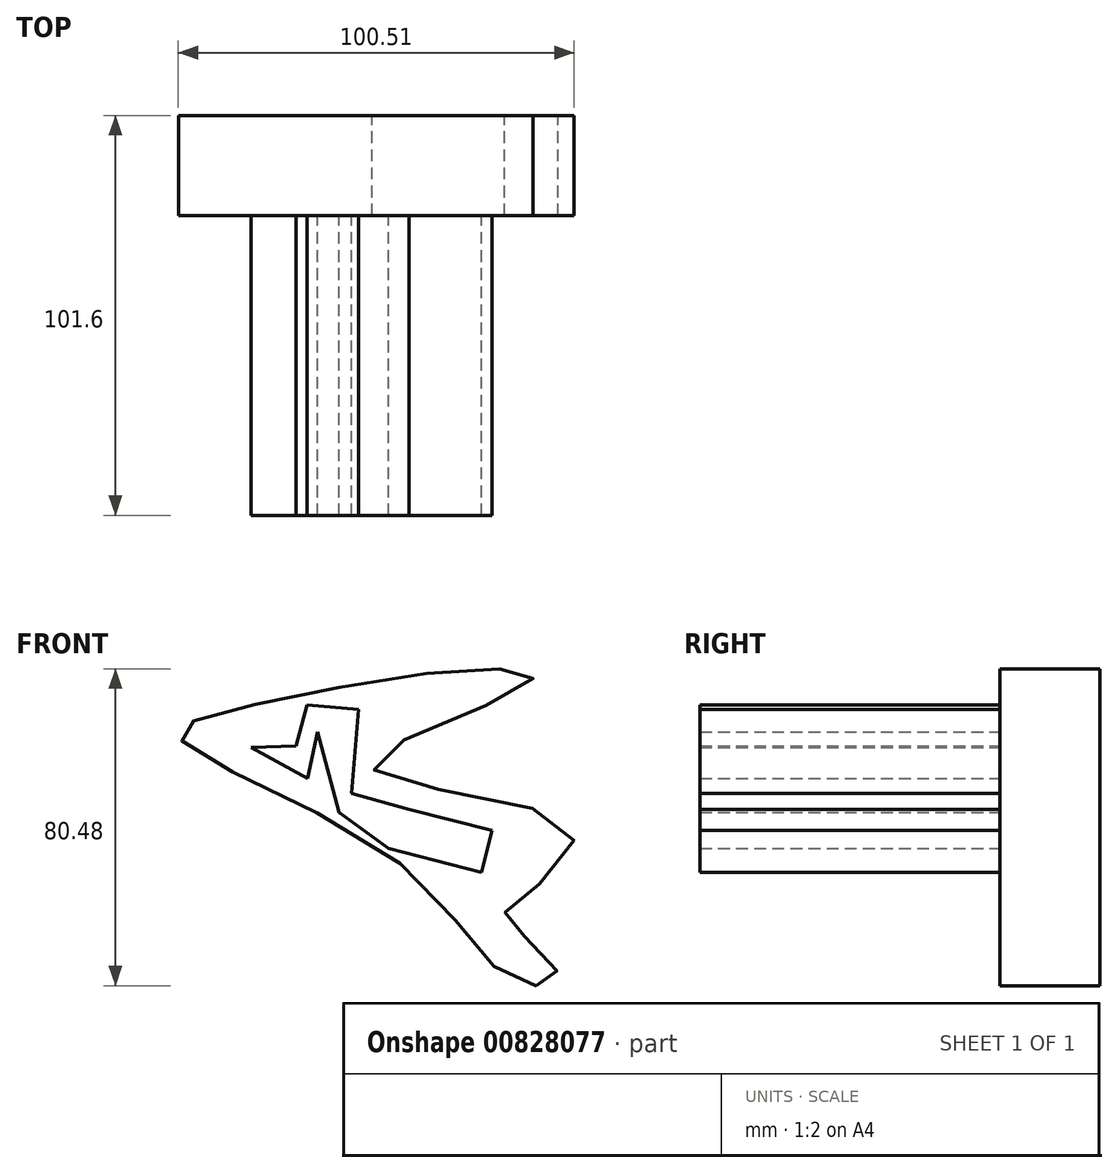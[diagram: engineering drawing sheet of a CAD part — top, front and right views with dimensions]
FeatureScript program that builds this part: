
annotation { "Feature Type Name" : "Feature", "Feature Type Description" : "" }
export const myFeature = defineFeature(function(context is Context, id is Id, definition is map)
    precondition{}
    {
        {
            var Q0;
            Q0=qCreatedBy(makeId("Front.planeOp"),FACE);
            var sketch = newSketch(context, id + "F0", { "sketchPlane" : qUnion([Q0])});
            skFitSpline(sketch, "E0", {"points": [v(0, 0) * mm, v(-56.1, 32.1) * mm, v(-39.9, 39.7) * mm, v(26.16, 49.34) * mm, v(33.34, 46.06) * mm, v(-7.08, 24.72) * mm, v(43.6, 8.72) * mm, v(28.2, -10.98) * mm, v(27.18, -14.46) * mm, v(40.1, -28.41) * mm, v(29.64, -30.06) * mm, v(0, 0) * mm]});
            skSolve(sketch);
        }
        {
            var Q0;
            Q0 = qSketchRegion(id + "F0", true);
            extrude(context, id + "F1", {"entities" : qUnion([Q0]), "depth" : 25.4 * mm, "offsetDistance" : 25.4 * mm});
        }
        {
            var Q0;
            Q0=makeQuery(id+"F1.opExtrude","CAP_FACE",FACE,{"disambiguationData":[OSD([sQuery(id+"F0.wireOp",EDGE,"E0")])],"isStart":false});
            var sketch = newSketch(context, id + "F2", { "sketchPlane" : qUnion([Q0])});
            skLineSegment(sketch, "E1", {"start": v(-37.83, 29.5) * mm, "end": v(-23.4, 21.62) * mm});
            skLineSegment(sketch, "E2", {"start": v(-23.4, 21.62) * mm, "end": v(-20.87, 33.34) * mm});
            skLineSegment(sketch, "E3", {"start": v(-20.87, 33.34) * mm, "end": v(-15.53, 13) * mm});
            skLineSegment(sketch, "E4", {"start": v(-15.53, 13) * mm, "end": v(-2.86, 3.79) * mm});
            skLineSegment(sketch, "E5", {"start": v(-2.86, 3.79) * mm, "end": v(20.74, -2.24) * mm});
            skLineSegment(sketch, "E6", {"start": v(20.74, -2.24) * mm, "end": v(23.43, 8.3) * mm});
            skLineSegment(sketch, "E7", {"start": v(23.43, 8.3) * mm, "end": v(2.27, 13.71) * mm});
            skLineSegment(sketch, "E8", {"start": v(2.27, 13.71) * mm, "end": v(-12.31, 17.78) * mm});
            skLineSegment(sketch, "E9", {"start": v(-12.31, 17.78) * mm, "end": v(-10.5, 39.15) * mm});
            skLineSegment(sketch, "E10", {"start": v(-10.5, 39.15) * mm, "end": v(-23.6, 40.26) * mm});
            skLineSegment(sketch, "E11", {"start": v(-23.6, 40.26) * mm, "end": v(-26.41, 29.85) * mm});
            skLineSegment(sketch, "E12", {"start": v(-26.41, 29.85) * mm, "end": v(-37.83, 29.5) * mm});
            skSolve(sketch);
        }
        {
            var Q0;
            Q0 = qSketchRegion(id + "F2", true);
            extrude(context, id + "F3", {"entities" : qUnion([Q0]), "operationType" : NewBodyOperationType.ADD, "depth" : 76.2 * mm, "offsetDistance" : 25.4 * mm});
        }
    });
